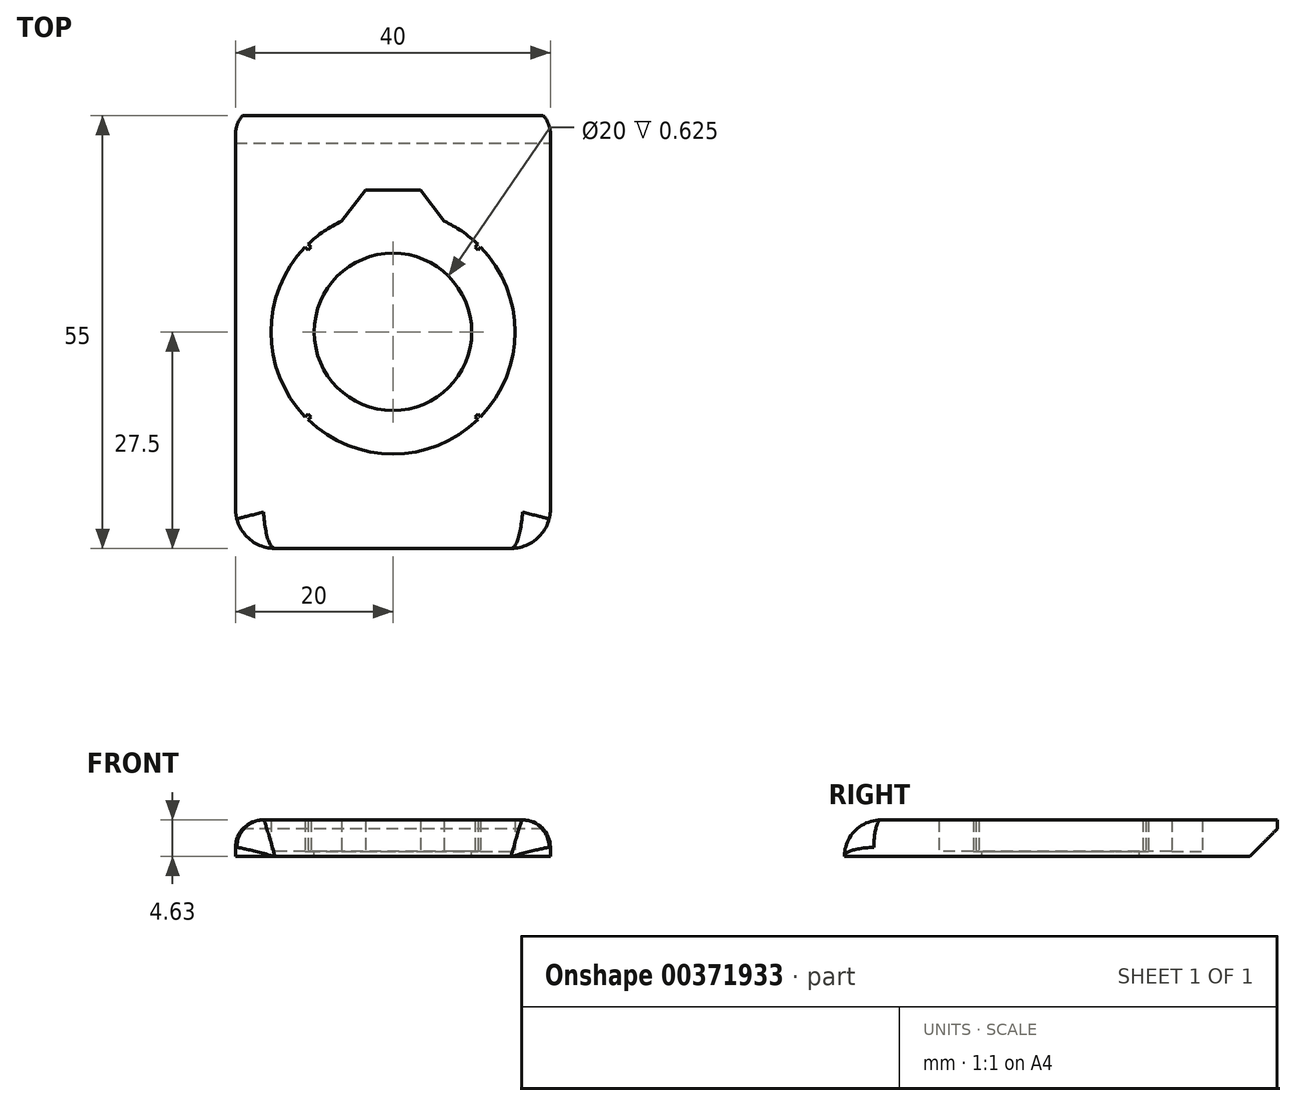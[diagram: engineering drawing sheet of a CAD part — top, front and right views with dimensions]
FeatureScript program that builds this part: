
annotation { "Feature Type Name" : "Feature", "Feature Type Description" : "" }
export const myFeature = defineFeature(function(context is Context, id is Id, definition is map)
    precondition{}
    {
        {
            var Q0;
            Q0=qCreatedBy(makeId("Top.planeOp"),FACE);
            var sketch = newSketch(context, id + "F0", { "sketchPlane" : qUnion([Q0])});
            skCircle(sketch, "E0", {"center": v(0, 0) * mm, "radius": 15.5 * mm});
            skLineSegment(sketch, "E1", {"start": v(-6.5, 14.07) * mm, "end": v(-3.5, 18) * mm});
            skLineSegment(sketch, "E2", {"start": v(-3.5, 18) * mm, "end": v(3.5, 18) * mm});
            skLineSegment(sketch, "E3", {"start": v(3.5, 18) * mm, "end": v(6.5, 14.07) * mm});
            skLineSegment(sketch, "E4", {"start": v(6.5, 14.07) * mm, "end": v(-6.5, 14.07) * mm, "construction": true});
            skPoint(sketch, "E5", {"position": v(0, 14.07) * mm});
            skPoint(sketch, "E6", {"position": v(0, 18) * mm});
            skLineSegment(sketch, "E7.bottom", {"start": v(-20, 27.5) * mm, "end": v(20, 27.5) * mm});
            skLineSegment(sketch, "E7.top", {"start": v(-15, -27.5) * mm, "end": v(15, -27.5) * mm});
            skLineSegment(sketch, "E7.left", {"start": v(-20, 27.5) * mm, "end": v(-20, -22.5) * mm});
            skLineSegment(sketch, "E7.right", {"start": v(20, 27.5) * mm, "end": v(20, -22.5) * mm});
            skPoint(sketch, "E8", {"position": v(-20, 0) * mm});
            skPoint(sketch, "E9", {"position": v(0, 15.5) * mm});
            skPoint(sketch, "E10", {"position": v(15.5, 0) * mm});
            skPoint(sketch, "E11", {"position": v(0, -15.5) * mm});
            skPoint(sketch, "E12", {"position": v(-15.5, 0) * mm});
            skPoint(sketch, "E13", {"position": v(-10.96, -10.96) * mm});
            skPoint(sketch, "E14", {"position": v(-10.96, 10.96) * mm});
            skPoint(sketch, "E15", {"position": v(10.96, 10.96) * mm});
            skPoint(sketch, "E16", {"position": v(10.96, -10.96) * mm});
            skLineSegment(sketch, "E17", {"start": v(-15.5, 0) * mm, "end": v(-10.96, 10.96) * mm, "construction": true});
            skLineSegment(sketch, "E18", {"start": v(-10.96, 10.96) * mm, "end": v(0, 15.5) * mm, "construction": true});
            skLineSegment(sketch, "E19", {"start": v(0, 15.5) * mm, "end": v(10.96, 10.96) * mm, "construction": true});
            skLineSegment(sketch, "E20", {"start": v(10.96, 10.96) * mm, "end": v(15.5, 0) * mm, "construction": true});
            skLineSegment(sketch, "E21", {"start": v(15.5, 0) * mm, "end": v(10.96, -10.96) * mm, "construction": true});
            skLineSegment(sketch, "E22", {"start": v(10.96, -10.96) * mm, "end": v(0, -15.5) * mm, "construction": true});
            skLineSegment(sketch, "E23", {"start": v(0, -15.5) * mm, "end": v(-10.96, -10.96) * mm, "construction": true});
            skLineSegment(sketch, "E24", {"start": v(-10.96, -10.96) * mm, "end": v(-15.5, 0) * mm, "construction": true});
            skLineSegment(sketch, "E25", {"start": v(10.78, 11.14) * mm, "end": v(11.14, 10.78) * mm, "construction": true});
            skLineSegment(sketch, "E26", {"start": v(11.14, 10.78) * mm, "end": v(10.78, 10.43) * mm});
            skLineSegment(sketch, "E27", {"start": v(10.78, 10.43) * mm, "end": v(10.43, 10.78) * mm});
            skLineSegment(sketch, "E28", {"start": v(10.43, 10.78) * mm, "end": v(10.78, 11.14) * mm});
            skPoint(sketch, "E29", {"position": v(10.6, 10.6) * mm});
            skLineSegment(sketch, "E30", {"start": v(10.6, 10.6) * mm, "end": v(10.96, 10.96) * mm, "construction": true});
            skLineSegment(sketch, "E31", {"start": v(10.78, -11.14) * mm, "end": v(11.14, -10.78) * mm, "construction": true});
            skLineSegment(sketch, "E32", {"start": v(10.78, -10.43) * mm, "end": v(11.14, -10.78) * mm});
            skLineSegment(sketch, "E33", {"start": v(10.78, -10.43) * mm, "end": v(10.43, -10.78) * mm});
            skLineSegment(sketch, "E34", {"start": v(10.78, -11.14) * mm, "end": v(10.43, -10.78) * mm});
            skLineSegment(sketch, "E35", {"start": v(10.96, -10.96) * mm, "end": v(10.6, -10.6) * mm, "construction": true});
            skLineSegment(sketch, "E36", {"start": v(-11.14, -10.78) * mm, "end": v(-10.78, -11.14) * mm, "construction": true});
            skLineSegment(sketch, "E37", {"start": v(-10.43, -10.78) * mm, "end": v(-10.78, -11.14) * mm});
            skLineSegment(sketch, "E38", {"start": v(-10.43, -10.78) * mm, "end": v(-10.78, -10.43) * mm});
            skLineSegment(sketch, "E39", {"start": v(-11.14, -10.78) * mm, "end": v(-10.78, -10.43) * mm});
            skLineSegment(sketch, "E40", {"start": v(-10.96, -10.96) * mm, "end": v(-10.6, -10.6) * mm, "construction": true});
            skLineSegment(sketch, "E41", {"start": v(-10.78, 11.14) * mm, "end": v(-11.14, 10.78) * mm, "construction": true});
            skLineSegment(sketch, "E42", {"start": v(-10.78, 10.43) * mm, "end": v(-11.14, 10.78) * mm});
            skLineSegment(sketch, "E43", {"start": v(-10.78, 10.43) * mm, "end": v(-10.43, 10.78) * mm});
            skLineSegment(sketch, "E44", {"start": v(-10.78, 11.14) * mm, "end": v(-10.43, 10.78) * mm});
            skLineSegment(sketch, "E45", {"start": v(-10.96, 10.96) * mm, "end": v(-10.6, 10.6) * mm, "construction": true});
            skPoint(sketch, "E46.visualSharp", {"position": v(-20, -27.5) * mm});
            skArc(sketch, "E46.filletArc", {"start": v(-20, -22.5) * mm, "mid": v(-18.54, -26.04) * mm, "end": v(-15, -27.5) * mm});
            skPoint(sketch, "E47.visualSharp", {"position": v(20, -27.5) * mm});
            skArc(sketch, "E47.filletArc", {"start": v(15, -27.5) * mm, "mid": v(18.54, -26.04) * mm, "end": v(20, -22.5) * mm});
            skSolve(sketch);
        }
        {
            var Q0;
            {var subQ0=sQuery(id+"F0.wireOp",EDGE,"E1");Q0=makeQuery(id+"F0.imprint","IMPRINT",FACE,{"disambiguationData":[TD([[makeQuery(id+"F0.imprint","IMPRINT",EDGE,{"derivedFrom":subQ0}),1.0]])]});}
            var Q1;
            {var subQ1=sQuery(id+"F0.wireOp",EDGE,"E26");Q1=makeQuery(id+"F0.imprint","IMPRINT",FACE,{"disambiguationData":[TD([[makeQuery(id+"F0.imprint","IMPRINT",EDGE,{"derivedFrom":subQ1}),1.0]])]});}
            var Q2;
            {var subQ0=sQuery(id+"F0.wireOp",EDGE,"E42");Q2=makeQuery(id+"F0.imprint","IMPRINT",FACE,{"disambiguationData":[TD([[makeQuery(id+"F0.imprint","IMPRINT",EDGE,{"derivedFrom":subQ0}),-1.0]])]});}
            var Q3;
            {var subQ0=sQuery(id+"F0.wireOp",EDGE,"E37");Q3=makeQuery(id+"F0.imprint","IMPRINT",FACE,{"disambiguationData":[TD([[makeQuery(id+"F0.imprint","IMPRINT",EDGE,{"derivedFrom":subQ0}),-1.0]])]});}
            var Q4;
            {var subQ0=sQuery(id+"F0.wireOp",EDGE,"E32");Q4=makeQuery(id+"F0.imprint","IMPRINT",FACE,{"disambiguationData":[TD([[makeQuery(id+"F0.imprint","IMPRINT",EDGE,{"derivedFrom":subQ0}),-1.0]])]});}
            var Q5;
            {var subQ0=sQuery(id+"F0.wireOp",EDGE,"E26");Q5=makeQuery(id+"F0.imprint","IMPRINT",FACE,{"disambiguationData":[TD([[makeQuery(id+"F0.imprint","IMPRINT",EDGE,{"derivedFrom":subQ0}),-1.0]])]});}
            var Q6;
            {var subQ0=sQuery(id+"F0.wireOp",EDGE,"E1");Q6=makeQuery(id+"F0.imprint","IMPRINT",FACE,{"disambiguationData":[TD([[makeQuery(id+"F0.imprint","IMPRINT",EDGE,{"derivedFrom":subQ0}),-1.0]])]});}
            extrude(context, id + "F1", {"entities" : qUnion([Q0, Q1, Q2, Q3, Q4, Q5, Q6]), "oppositeDirection" : true, "depth" : 0.62 * mm});
        }
        {
            var Q0;
            Q0=makeQuery(id+"F0.imprint","IMPRINT",FACE,{"disambiguationData":[TD([[makeQuery(id+"F0.imprint","IMPRINT",EDGE,{"derivedFrom":sQuery(id+"F0.wireOp",EDGE,"E41")}),1.0]])]});
            var Q1;
            Q1=makeQuery(id+"F0.imprint","IMPRINT",FACE,{"disambiguationData":[TD([[makeQuery(id+"F0.imprint","IMPRINT",EDGE,{"derivedFrom":sQuery(id+"F0.wireOp",EDGE,"E25")}),-1.0]])]});
            var Q2;
            Q2=makeQuery(id+"F0.imprint","IMPRINT",FACE,{"disambiguationData":[TD([[makeQuery(id+"F0.imprint","IMPRINT",EDGE,{"derivedFrom":sQuery(id+"F0.wireOp",EDGE,"E31")}),1.0]])]});
            var Q3;
            Q3=makeQuery(id+"F0.imprint","IMPRINT",FACE,{"disambiguationData":[TD([[makeQuery(id+"F0.imprint","IMPRINT",EDGE,{"derivedFrom":sQuery(id+"F0.wireOp",EDGE,"E36")}),1.0]])]});
            var Q4;
            {var subQ0=sQuery(id+"F0.wireOp",EDGE,"E1");Q4=makeQuery(id+"F0.imprint","IMPRINT",FACE,{"disambiguationData":[TD([[makeQuery(id+"F0.imprint","IMPRINT",EDGE,{"derivedFrom":subQ0}),1.0]])]});}
            var Q5;
            {var subQ0=sQuery(id+"F0.wireOp",EDGE,"E42");Q5=makeQuery(id+"F0.imprint","IMPRINT",FACE,{"disambiguationData":[TD([[makeQuery(id+"F0.imprint","IMPRINT",EDGE,{"derivedFrom":subQ0}),-1.0]])]});}
            var Q6;
            {var subQ0=sQuery(id+"F0.wireOp",EDGE,"E26");Q6=makeQuery(id+"F0.imprint","IMPRINT",FACE,{"disambiguationData":[TD([[makeQuery(id+"F0.imprint","IMPRINT",EDGE,{"derivedFrom":subQ0}),-1.0]])]});}
            var Q7;
            {var subQ0=sQuery(id+"F0.wireOp",EDGE,"E37");Q7=makeQuery(id+"F0.imprint","IMPRINT",FACE,{"disambiguationData":[TD([[makeQuery(id+"F0.imprint","IMPRINT",EDGE,{"derivedFrom":subQ0}),-1.0]])]});}
            var Q8;
            {var subQ0=sQuery(id+"F0.wireOp",EDGE,"E32");Q8=makeQuery(id+"F0.imprint","IMPRINT",FACE,{"disambiguationData":[TD([[makeQuery(id+"F0.imprint","IMPRINT",EDGE,{"derivedFrom":subQ0}),-1.0]])]});}
            var Q9;
            Q9 = qSketchRegion(id + "F3", true);
            extrude(context, id + "F2", {"entities" : qUnion([Q0, Q1, Q2, Q3, Q4, Q5, Q6, Q7, Q8, Q9]), "operationType" : NewBodyOperationType.ADD, "depth" : 4 * mm});
        }
        {
            var Q0;
            Q0=makeQuery(id+"F1.opExtrude","CAP_FACE",FACE,{"disambiguationData":[OSD([sQuery(id+"F0.wireOp",EDGE,"E7.bottom"),sQuery(id+"F0.wireOp",EDGE,"E7.top"),sQuery(id+"F0.wireOp",EDGE,"E7.left"),sQuery(id+"F0.wireOp",EDGE,"E7.right")])],"isStart":true});
            var sketch = newSketch(context, id + "F3", { "sketchPlane" : qUnion([Q0])});
            skCircle(sketch, "E48", {"center": v(0, 0) * mm, "radius": 10 * mm});
            skSolve(sketch);
        }
        {
            var Q0;
            Q0=makeQuery(id+"F3.imprint","IMPRINT",FACE,{"disambiguationData":[TD([[makeQuery(id+"F3.imprint","IMPRINT",EDGE,{"derivedFrom":sQuery(id+"F3.wireOp",EDGE,"E48")}),1.0]])]});
            extrude(context, id + "F4", {"entities" : qUnion([Q0]), "operationType" : NewBodyOperationType.REMOVE, "oppositeDirection" : true, "depth" : 25 * mm});
        }
        {
            var Q0;
            Q0=makeQuery(id+"F1.opExtrude","CAP_EDGE",EDGE,{"disambiguationData":[OSD([sQuery(id+"F0.wireOp",EDGE,"E7.bottom")])],"isStart":false});
            chamfer(context, id + "F5", {"entities" : qUnion([Q0]), "chamferType" : ChamferType.OFFSET_ANGLE, "width" : 3.5 * mm, "oppositeDirection" : false, "angle" : 45 * degree, "tangentPropagation" : true});
        }
        {
            var Q0;
            Q0=makeQuery(id+"F2.opExtrude","CAP_EDGE",EDGE,{"disambiguationData":[OSD([sQuery(id+"F0.wireOp",EDGE,"E7.left")])],"isStart":false});
            var Q1;
            Q1=makeQuery(id+"F2.opExtrude","CAP_EDGE",EDGE,{"disambiguationData":[OSD([sQuery(id+"F0.wireOp",EDGE,"E7.right")])],"isStart":false});
            fillet(context, id + "F6", {"entities" : qUnion([Q0, Q1]), "radius" : 3.5 * mm, "allowEdgeOverflow" : false});
        }
        {
            var Q0;
            Q0=makeQuery(id+"F2.opExtrude","CAP_EDGE",EDGE,{"disambiguationData":[OSD([sQuery(id+"F0.wireOp",EDGE,"E7.top")])],"isStart":false});
            fillet(context, id + "F7", {"entities" : qUnion([Q0]), "radius" : 4.62 * mm, "tangentPropagation" : true, "allowEdgeOverflow" : false});
        }
    });
